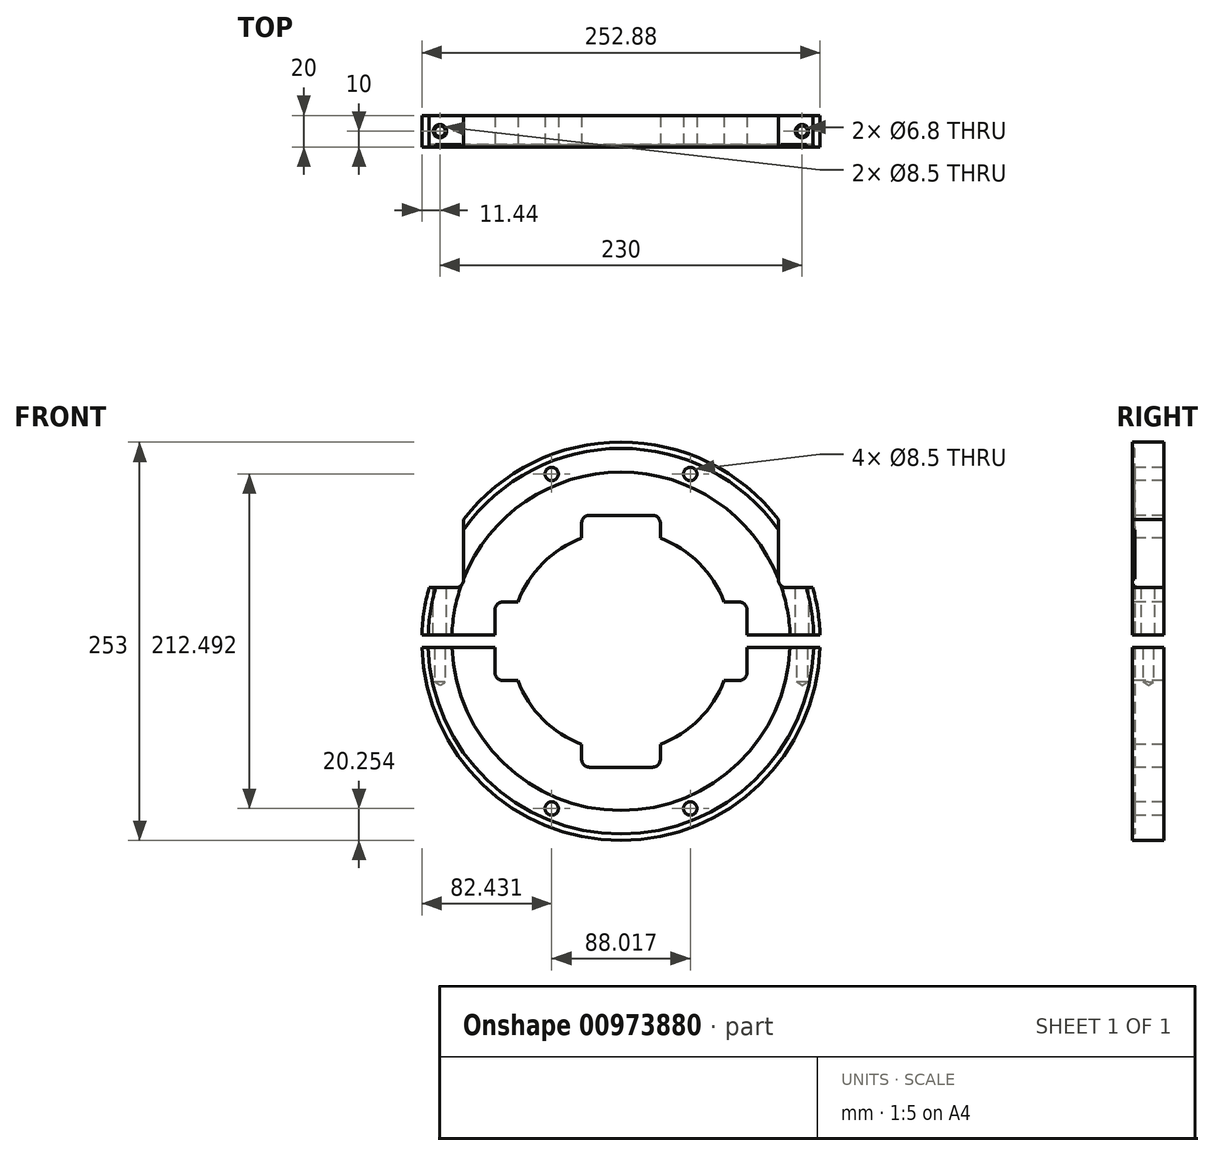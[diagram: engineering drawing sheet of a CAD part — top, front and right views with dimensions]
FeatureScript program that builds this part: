
annotation { "Feature Type Name" : "Feature", "Feature Type Description" : "" }
export const myFeature = defineFeature(function(context is Context, id is Id, definition is map)
    precondition{}
    {
        {
            var Q0;
            Q0=qCreatedBy(makeId("Right.planeOp"),FACE);
            var sketch = newSketch(context, id + "F0", { "sketchPlane" : qUnion([Q0])});
            skLineSegment(sketch, "E0", {"start": v(0, 126.5) * mm, "end": v(20, 126.5) * mm});
            skLineSegment(sketch, "E1", {"start": v(0, 126.5) * mm, "end": v(0, 122.5) * mm});
            skLineSegment(sketch, "E2", {"start": v(0, 122.5) * mm, "end": v(1.5, 122.5) * mm});
            skLineSegment(sketch, "E3", {"start": v(1.5, 122.5) * mm, "end": v(1.5, 107.5) * mm});
            skLineSegment(sketch, "E4", {"start": v(1.5, 107.5) * mm, "end": v(0, 107.5) * mm});
            skLineSegment(sketch, "E5", {"start": v(0, 107.5) * mm, "end": v(0, 70.1) * mm});
            skLineSegment(sketch, "E6", {"start": v(0, 70.1) * mm, "end": v(20, 70.1) * mm});
            skLineSegment(sketch, "E7", {"start": v(20, 126.5) * mm, "end": v(20, 70.1) * mm});
            skLineSegment(sketch, "E8", {"start": v(0, 0) * mm, "end": v(20, 0) * mm, "construction": true});
            skSolve(sketch);
        }
        {
            var Q0;
            Q0=qSketchRegion(id+"F0",true);
            var Q1;
            Q1=sQuery(id+"F0.wireOp",EDGE,"E8");
            revolve(context, id + "F1", {"surfaceOperationType" : NewSurfaceOperationType.NEW, "entities" : qUnion([Q0]), "axis" : qUnion([Q1]), "revolveType" : RevolveType.FULL});
        }
        {
            var Q0;
            Q0=qCreatedBy(makeId("Front.planeOp"),FACE);
            var sketch = newSketch(context, id + "F2", { "sketchPlane" : qUnion([Q0])});
            skLineSegment(sketch, "E9.bottom", {"start": v(-126.5, 4) * mm, "end": v(126.5, 4) * mm});
            skLineSegment(sketch, "E9.top", {"start": v(-126.5, -4) * mm, "end": v(126.5, -4) * mm});
            skLineSegment(sketch, "E9.left", {"start": v(-126.5, 4) * mm, "end": v(-126.5, -4) * mm});
            skLineSegment(sketch, "E9.right", {"start": v(126.5, 4) * mm, "end": v(126.5, -4) * mm});
            skLineSegment(sketch, "E10.bottom", {"start": v(-180, 34) * mm, "end": v(-100, 34) * mm});
            skLineSegment(sketch, "E10.top", {"start": v(-180, 114) * mm, "end": v(-100, 114) * mm});
            skLineSegment(sketch, "E10.left", {"start": v(-180, 34) * mm, "end": v(-180, 114) * mm});
            skLineSegment(sketch, "E10.right", {"start": v(-100, 34) * mm, "end": v(-100, 114) * mm});
            skLineSegment(sketch, "E11.bottom", {"start": v(180, 34) * mm, "end": v(100, 34) * mm});
            skLineSegment(sketch, "E11.top", {"start": v(180, 114) * mm, "end": v(100, 114) * mm});
            skLineSegment(sketch, "E11.left", {"start": v(180, 34) * mm, "end": v(180, 114) * mm});
            skLineSegment(sketch, "E11.right", {"start": v(100, 34) * mm, "end": v(100, 114) * mm});
            skCircle(sketch, "E12", {"center": v(0, 0) * mm, "radius": 115 * mm, "construction": true});
            skLineSegment(sketch, "E13", {"start": v(0, 0) * mm, "end": v(-44, 106.25) * mm, "construction": true});
            skLineSegment(sketch, "E14", {"start": v(0, 0) * mm, "end": v(44, 106.25) * mm, "construction": true});
            skLineSegment(sketch, "E15", {"start": v(0, 0) * mm, "end": v(-44, -106.25) * mm, "construction": true});
            skLineSegment(sketch, "E16", {"start": v(0, 0) * mm, "end": v(44, -106.25) * mm, "construction": true});
            skCircle(sketch, "E17", {"center": v(-44, 106.25) * mm, "radius": 4.25 * mm});
            skCircle(sketch, "E18", {"center": v(44, 106.25) * mm, "radius": 4.25 * mm});
            skCircle(sketch, "E19", {"center": v(-44, -106.25) * mm, "radius": 4.25 * mm});
            skCircle(sketch, "E20", {"center": v(44, -106.25) * mm, "radius": 4.25 * mm});
            skLineSegment(sketch, "E21.bottom", {"start": v(-25, 80) * mm, "end": v(25, 80) * mm});
            skLineSegment(sketch, "E21.top", {"start": v(-25, -80) * mm, "end": v(25, -80) * mm});
            skLineSegment(sketch, "E21.left", {"start": v(-25, 80) * mm, "end": v(-25, -80) * mm});
            skLineSegment(sketch, "E21.right", {"start": v(25, 80) * mm, "end": v(25, -80) * mm});
            skLineSegment(sketch, "E22.bottom", {"start": v(-80, -25) * mm, "end": v(80, -25) * mm});
            skLineSegment(sketch, "E22.top", {"start": v(-80, 25) * mm, "end": v(80, 25) * mm});
            skLineSegment(sketch, "E22.left", {"start": v(-80, -25) * mm, "end": v(-80, 25) * mm});
            skLineSegment(sketch, "E22.right", {"start": v(80, -25) * mm, "end": v(80, 25) * mm});
            skSolve(sketch);
        }
        {
            var Q0;
            Q0=qSketchRegion(id+"F2",true);
            extrude(context, id + "F3", {"entities" : qUnion([Q0]), "operationType" : NewBodyOperationType.REMOVE, "oppositeDirection" : true, "depth" : 25 * mm, "offsetDistance" : 25 * mm});
        }
        {
            var Q0;
            Q0=qCreatedBy(makeId("Top.planeOp"),FACE);
            var sketch = newSketch(context, id + "F4", { "sketchPlane" : qUnion([Q0])});
            skLineSegment(sketch, "E23", {"start": v(-115, 10) * mm, "end": v(115, 10) * mm, "construction": true});
            skSolve(sketch);
        }
        {
            var Q0;
            Q0=sQuery(id+"F4.wireOp",VERTEX,"E23.start");
            var Q1;
            Q1=sQuery(id+"F4.wireOp",VERTEX,"E23.end");
            var Q2;
            Q2=makeQuery(id+"F3.boolean.opBoolean","SPLIT",BODY,{"disambiguationData":[OD(0.0)],"derivedFrom":makeQuery(id+"F1.opRevolve","SWEPT_BODY",BODY,{"disambiguationData":[OSD([sQuery(id+"F0.wireOp",EDGE,"E0"),sQuery(id+"F0.wireOp",EDGE,"E1"),sQuery(id+"F0.wireOp",EDGE,"E2"),sQuery(id+"F0.wireOp",EDGE,"E3"),sQuery(id+"F0.wireOp",EDGE,"E4"),sQuery(id+"F0.wireOp",EDGE,"E5"),sQuery(id+"F0.wireOp",EDGE,"E6"),sQuery(id+"F0.wireOp",EDGE,"8ZPzUNCr-arfV-oxd5-zyJ7-DsxsbWkkWO5k"),sQuery(id+"F0.wireOp",EDGE,"r5Ri2eYd-TK7H-3AMs-LwIH-2MvLVqk5ScA1"),sQuery(id+"F0.wireOp",EDGE,"uuWHYqOO-eIgU-OGWJ-oPIl-c3udvMWTDMT0"),sQuery(id+"F0.wireOp",EDGE,"spNpiRdv-UxyK-27CQ-Z1uT-EOWI6jPaa9Q3"),sQuery(id+"F0.wireOp",EDGE,"VSwbT7gE-iAiO-8DaZ-YpUb-RmRVHXjJfYn9"),sQuery(id+"F0.wireOp",EDGE,"raDsLyMx-sMko-872A-1KDE-koLtCoFYT9ND"),sQuery(id+"F0.wireOp",EDGE,"t46iTn9E-MaXW-ciSI-CEys-LNGwPZW84j7c"),sQuery(id+"F0.wireOp",EDGE,"wQwgna7D-6bcO-KLk3-nCw8-YYEir8QgGa18"),sQuery(id+"F0.wireOp",EDGE,"BB6GjwT5-xiiA-J7Oq-Vah7-FBMgJwNET3xY"),sQuery(id+"F0.wireOp",EDGE,"3KHcW86Q-H1JC-HKv4-5Ryt-jvmL1GMle0qr"),sQuery(id+"F0.wireOp",EDGE,"zh9PdE1M-VMSQ-mWXI-m2Wo-egHtLExWAzZm"),sQuery(id+"F0.wireOp",EDGE,"3qDCw8pE-qAM9-JolM-J0dQ-s85WylCnzzzp"),sQuery(id+"F0.wireOp",EDGE,"E7")])]})});
            hole(context, id + "F5", {"style" : HoleStyle.SIMPLE, "endStyle" : HoleEndStyle.BLIND, "standardTappedOrClearance" : lookupTablePath({ "standard" : "ISO", "engagement" : "75%", "pitch" : "1.25 mm", "size" : "M8", "type" : "Tapped" }), "standardBlindInLast" : lookupTablePath({ "standard" : "ISO", "fit" : "Normal", "engagement" : "75%", "pitch" : "1.25 mm", "size" : "M8", "type" : "Clearance & tapped" }), "holeDiameter" : 6.8 * mm, "majorDiameter" : 8 * mm, "showTappedDepth" : true, "holeDepth" : 22 * mm, "tappedDepth" : 17 * mm, "tapClearance" : 4, "locations" : qUnion([Q0, Q1]), "scope" : qUnion([Q2])});
        }
        {
            var Q0;
            Q0=sQuery(id+"F4.wireOp",VERTEX,"E23.start");
            var Q1;
            Q1=sQuery(id+"F4.wireOp",VERTEX,"E23.end");
            var Q2;
            Q2=makeQuery(id+"F3.boolean.opBoolean","SPLIT",BODY,{"disambiguationData":[OD(1.0)],"derivedFrom":makeQuery(id+"F1.opRevolve","SWEPT_BODY",BODY,{"disambiguationData":[OSD([sQuery(id+"F0.wireOp",EDGE,"E0"),sQuery(id+"F0.wireOp",EDGE,"E1"),sQuery(id+"F0.wireOp",EDGE,"E2"),sQuery(id+"F0.wireOp",EDGE,"E3"),sQuery(id+"F0.wireOp",EDGE,"E4"),sQuery(id+"F0.wireOp",EDGE,"E5"),sQuery(id+"F0.wireOp",EDGE,"E6"),sQuery(id+"F0.wireOp",EDGE,"8ZPzUNCr-arfV-oxd5-zyJ7-DsxsbWkkWO5k"),sQuery(id+"F0.wireOp",EDGE,"r5Ri2eYd-TK7H-3AMs-LwIH-2MvLVqk5ScA1"),sQuery(id+"F0.wireOp",EDGE,"uuWHYqOO-eIgU-OGWJ-oPIl-c3udvMWTDMT0"),sQuery(id+"F0.wireOp",EDGE,"spNpiRdv-UxyK-27CQ-Z1uT-EOWI6jPaa9Q3"),sQuery(id+"F0.wireOp",EDGE,"VSwbT7gE-iAiO-8DaZ-YpUb-RmRVHXjJfYn9"),sQuery(id+"F0.wireOp",EDGE,"raDsLyMx-sMko-872A-1KDE-koLtCoFYT9ND"),sQuery(id+"F0.wireOp",EDGE,"t46iTn9E-MaXW-ciSI-CEys-LNGwPZW84j7c"),sQuery(id+"F0.wireOp",EDGE,"wQwgna7D-6bcO-KLk3-nCw8-YYEir8QgGa18"),sQuery(id+"F0.wireOp",EDGE,"BB6GjwT5-xiiA-J7Oq-Vah7-FBMgJwNET3xY"),sQuery(id+"F0.wireOp",EDGE,"3KHcW86Q-H1JC-HKv4-5Ryt-jvmL1GMle0qr"),sQuery(id+"F0.wireOp",EDGE,"zh9PdE1M-VMSQ-mWXI-m2Wo-egHtLExWAzZm"),sQuery(id+"F0.wireOp",EDGE,"3qDCw8pE-qAM9-JolM-J0dQ-s85WylCnzzzp"),sQuery(id+"F0.wireOp",EDGE,"E7")])]})});
            hole(context, id + "F6", {"style" : HoleStyle.SIMPLE, "endStyle" : HoleEndStyle.THROUGH, "oppositeDirection" : true, "holeDiameter" : 8.5 * mm, "majorDiameter" : 8 * mm, "tappedDepth" : 16 * mm, "tapClearance" : 5, "locations" : qUnion([Q0, Q1]), "scope" : qUnion([Q2])});
        }
        {
            var Q0;
            Q0=makeQuery(id+"F3.boolean.opBoolean","COPY",EDGE,{"derivedFrom":makeQuery(id+"F3.opExtrude","SWEPT_EDGE",EDGE,{"disambiguationData":[OSD([sQuery(id+"F2.wireOp",EDGE,"E22.bottom"),sQuery(id+"F2.wireOp",EDGE,"E22.left")])]})});
            var Q1;
            Q1=makeQuery(id+"F3.boolean.opBoolean","COPY",EDGE,{"derivedFrom":makeQuery(id+"F3.opExtrude","SWEPT_EDGE",EDGE,{"disambiguationData":[OSD([sQuery(id+"F2.wireOp",EDGE,"E22.top"),sQuery(id+"F2.wireOp",EDGE,"E22.left")])]})});
            var Q2;
            Q2=makeQuery(id+"F3.boolean.opBoolean","COPY",EDGE,{"derivedFrom":makeQuery(id+"F3.opExtrude","SWEPT_EDGE",EDGE,{"disambiguationData":[OSD([sQuery(id+"F2.wireOp",EDGE,"E21.bottom"),sQuery(id+"F2.wireOp",EDGE,"E21.left")])]})});
            var Q3;
            Q3=makeQuery(id+"F3.boolean.opBoolean","COPY",EDGE,{"derivedFrom":makeQuery(id+"F3.opExtrude","SWEPT_EDGE",EDGE,{"disambiguationData":[OSD([sQuery(id+"F2.wireOp",EDGE,"E21.bottom"),sQuery(id+"F2.wireOp",EDGE,"E21.right")])]})});
            var Q4;
            Q4=makeQuery(id+"F3.boolean.opBoolean","COPY",EDGE,{"derivedFrom":makeQuery(id+"F3.opExtrude","SWEPT_EDGE",EDGE,{"disambiguationData":[OSD([sQuery(id+"F2.wireOp",EDGE,"E22.top"),sQuery(id+"F2.wireOp",EDGE,"E22.right")])]})});
            var Q5;
            Q5=makeQuery(id+"F3.boolean.opBoolean","COPY",EDGE,{"derivedFrom":makeQuery(id+"F3.opExtrude","SWEPT_EDGE",EDGE,{"disambiguationData":[OSD([sQuery(id+"F2.wireOp",EDGE,"E22.bottom"),sQuery(id+"F2.wireOp",EDGE,"E22.right")])]})});
            var Q6;
            Q6=makeQuery(id+"F3.boolean.opBoolean","COPY",EDGE,{"derivedFrom":makeQuery(id+"F3.opExtrude","SWEPT_EDGE",EDGE,{"disambiguationData":[OSD([sQuery(id+"F2.wireOp",EDGE,"E21.top"),sQuery(id+"F2.wireOp",EDGE,"E21.right")])]})});
            var Q7;
            Q7=makeQuery(id+"F3.boolean.opBoolean","COPY",EDGE,{"derivedFrom":makeQuery(id+"F3.opExtrude","SWEPT_EDGE",EDGE,{"disambiguationData":[OSD([sQuery(id+"F2.wireOp",EDGE,"E21.top"),sQuery(id+"F2.wireOp",EDGE,"E21.left")])]})});
            var Q8;
            Q8=makeQuery(id+"F3.boolean.opBoolean","COPY",EDGE,{"derivedFrom":makeQuery(id+"F3.opExtrude","SWEPT_EDGE",EDGE,{"disambiguationData":[OSD([sQuery(id+"F2.wireOp",EDGE,"E10.bottom"),sQuery(id+"F2.wireOp",EDGE,"E10.right")])]})});
            var Q9;
            Q9=makeQuery(id+"F3.boolean.opBoolean","COPY",EDGE,{"derivedFrom":makeQuery(id+"F3.opExtrude","SWEPT_EDGE",EDGE,{"disambiguationData":[OSD([sQuery(id+"F2.wireOp",EDGE,"E11.bottom"),sQuery(id+"F2.wireOp",EDGE,"E11.right")])]})});
            fillet(context, id + "F7", {"entities" : qUnion([Q0, Q1, Q2, Q3, Q4, Q5, Q6, Q7, Q8, Q9]), "radius" : 5 * mm, "tangentPropagation" : true, "allowEdgeOverflow" : false});
        }
    });
